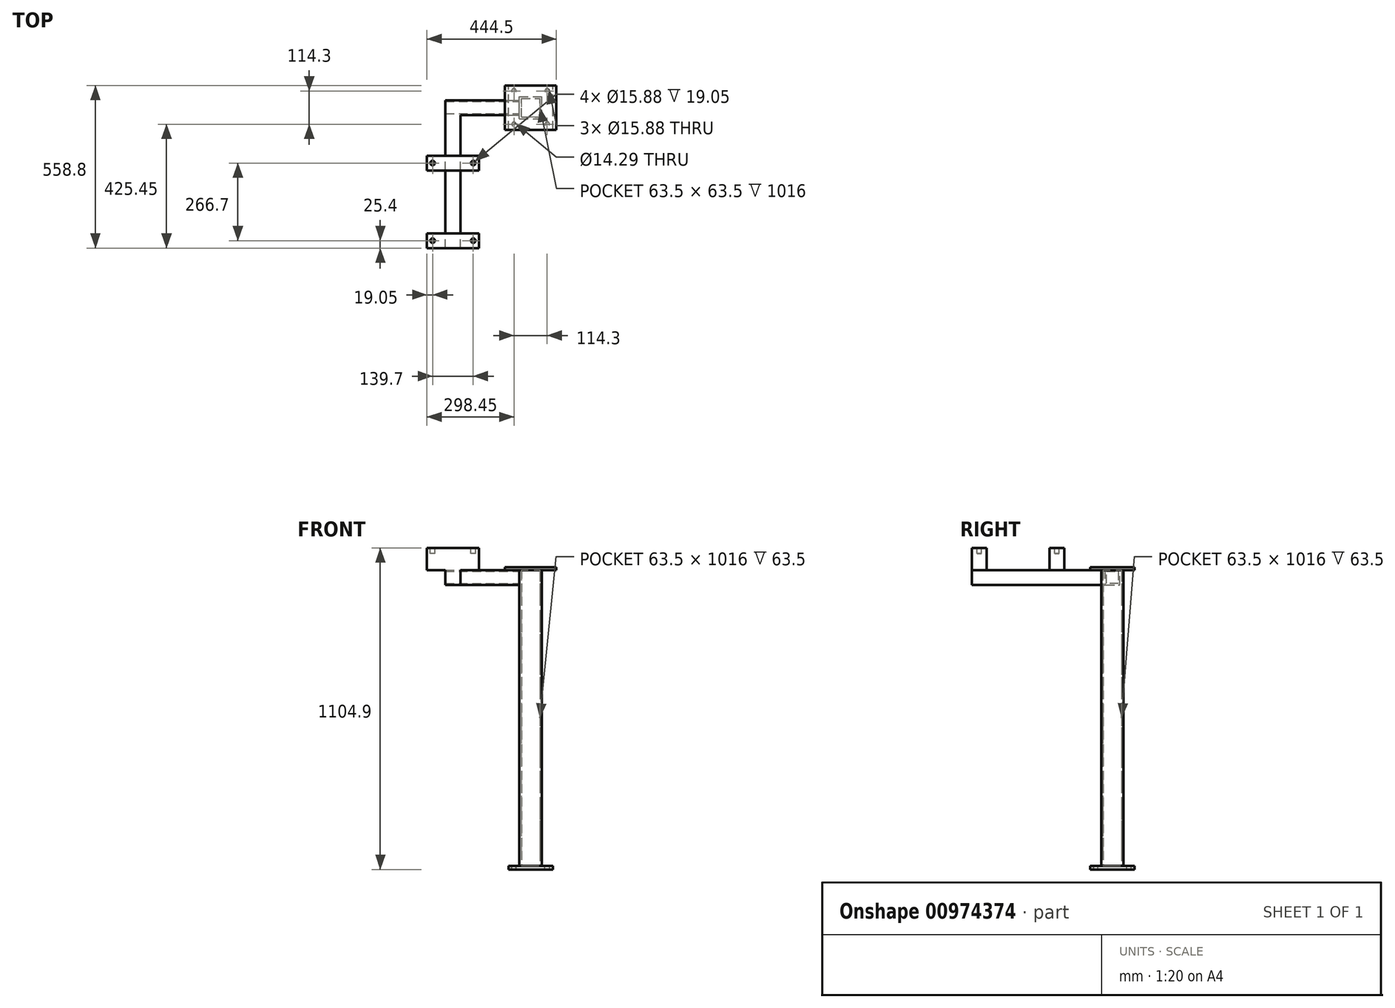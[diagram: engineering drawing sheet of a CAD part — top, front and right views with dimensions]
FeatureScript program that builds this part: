
annotation { "Feature Type Name" : "Feature", "Feature Type Description" : "" }
export const myFeature = defineFeature(function(context is Context, id is Id, definition is map)
    precondition{}
    {
        {
            var Q0;
            Q0=qCreatedBy(makeId("Top.planeOp"),FACE);
            var sketch = newSketch(context, id + "F0", { "sketchPlane" : qUnion([Q0])});
            skLineSegment(sketch, "E0.bottom", {"start": v(0, 0) * mm, "end": v(152.4, 0) * mm});
            skLineSegment(sketch, "E0.top", {"start": v(0, 152.4) * mm, "end": v(152.4, 152.4) * mm});
            skLineSegment(sketch, "E0.left", {"start": v(0, 0) * mm, "end": v(0, 152.4) * mm});
            skLineSegment(sketch, "E0.right", {"start": v(152.4, 0) * mm, "end": v(152.4, 152.4) * mm});
            skSolve(sketch);
        }
        {
            var Q0;
            Q0 = qSketchRegion(id + "F0", true);
            extrude(context, id + "F1", {"entities" : qUnion([Q0]), "depth" : 12.7 * mm, "offsetDistance" : 25.4 * mm});
        }
        {
            var Q0;
            Q0=makeQuery(id+"F1.opExtrude","CAP_FACE",FACE,{"disambiguationData":[OSD([sQuery(id+"F0.wireOp",EDGE,"E0.bottom"),sQuery(id+"F0.wireOp",EDGE,"E0.top"),sQuery(id+"F0.wireOp",EDGE,"E0.left"),sQuery(id+"F0.wireOp",EDGE,"E0.right")])],"isStart":false});
            var sketch = newSketch(context, id + "F2", { "sketchPlane" : qUnion([Q0])});
            skLineSegment(sketch, "E1.bottom", {"start": v(38.1, 38.1) * mm, "end": v(114.3, 38.1) * mm});
            skLineSegment(sketch, "E1.top", {"start": v(38.1, 114.3) * mm, "end": v(114.3, 114.3) * mm});
            skLineSegment(sketch, "E1.left", {"start": v(38.1, 38.1) * mm, "end": v(38.1, 114.3) * mm});
            skLineSegment(sketch, "E1.right", {"start": v(114.3, 38.1) * mm, "end": v(114.3, 114.3) * mm});
            skLineSegment(sketch, "E2.bottom", {"start": v(44.45, 44.45) * mm, "end": v(107.95, 44.45) * mm});
            skLineSegment(sketch, "E2.top", {"start": v(44.45, 107.95) * mm, "end": v(107.95, 107.95) * mm});
            skLineSegment(sketch, "E2.left", {"start": v(44.45, 44.45) * mm, "end": v(44.45, 107.95) * mm});
            skLineSegment(sketch, "E2.right", {"start": v(107.95, 44.45) * mm, "end": v(107.95, 107.95) * mm});
            skSolve(sketch);
        }
        {
            var Q0;
            Q0 = qSketchRegion(id + "F2", true);
            extrude(context, id + "F3", {"entities" : qUnion([Q0]), "operationType" : NewBodyOperationType.ADD, "depth" : 1016 * mm, "offsetDistance" : 25.4 * mm});
        }
        {
            var Q0;
            Q0=makeQuery(id+"F3.opExtrude","SWEPT_FACE",FACE,{"disambiguationData":[OSD([sQuery(id+"F2.wireOp",EDGE,"E1.left")])]});
            var sketch = newSketch(context, id + "F4", { "sketchPlane" : qUnion([Q0])});
            skLineSegment(sketch, "E3", {"start": v(-114.3, 1028.7) * mm, "end": v(-101.6, 1028.7) * mm});
            skLineSegment(sketch, "E4", {"start": v(-101.6, 1028.7) * mm, "end": v(0, 1028.7) * mm});
            skLineSegment(sketch, "E5", {"start": v(-101.6, 1028.7) * mm, "end": v(-50.8, 1028.7) * mm});
            skLineSegment(sketch, "E6", {"start": v(-50.8, 1028.7) * mm, "end": v(-50.8, 977.9) * mm});
            skLineSegment(sketch, "E7", {"start": v(-50.8, 977.9) * mm, "end": v(-101.6, 977.9) * mm});
            skLineSegment(sketch, "E8", {"start": v(-101.6, 977.9) * mm, "end": v(-101.6, 1028.7) * mm});
            skLineSegment(sketch, "E9", {"start": v(-101.6, 1028.7) * mm, "end": v(-101.6, 1023.94) * mm});
            skLineSegment(sketch, "E10", {"start": v(-101.6, 1023.94) * mm, "end": v(-96.84, 1023.94) * mm});
            skLineSegment(sketch, "E11", {"start": v(-96.84, 1023.94) * mm, "end": v(-96.84, 982.66) * mm});
            skLineSegment(sketch, "E12", {"start": v(-96.84, 982.66) * mm, "end": v(-55.56, 982.66) * mm});
            skLineSegment(sketch, "E13", {"start": v(-55.56, 982.66) * mm, "end": v(-55.56, 1023.94) * mm});
            skLineSegment(sketch, "E14", {"start": v(-55.56, 1023.94) * mm, "end": v(-96.84, 1023.94) * mm});
            skSolve(sketch);
        }
        {
            var Q0;
            Q0 = qSketchRegion(id + "F4", true);
            extrude(context, id + "F5", {"entities" : qUnion([Q0]), "operationType" : NewBodyOperationType.ADD, "depth" : 254 * mm, "offsetDistance" : 25.4 * mm});
        }
        {
            var Q0;
            Q0=makeQuery(id+"F5.opExtrude","SWEPT_FACE",FACE,{"disambiguationData":[OSD([sQuery(id+"F4.wireOp",EDGE,"E6")])]});
            var sketch = newSketch(context, id + "F6", { "sketchPlane" : qUnion([Q0])});
            skLineSegment(sketch, "E15", {"start": v(-215.9, 1028.7) * mm, "end": v(-165.1, 1028.7) * mm});
            skLineSegment(sketch, "E16", {"start": v(-165.1, 1028.7) * mm, "end": v(-165.1, 977.9) * mm});
            skLineSegment(sketch, "E17", {"start": v(-165.1, 977.9) * mm, "end": v(-215.9, 977.9) * mm});
            skLineSegment(sketch, "E18", {"start": v(-215.9, 977.9) * mm, "end": v(-215.9, 1028.7) * mm});
            skSolve(sketch);
        }
        {
            var Q0;
            Q0 = qSketchRegion(id + "F6", true);
            extrude(context, id + "F7", {"entities" : qUnion([Q0]), "operationType" : NewBodyOperationType.ADD, "depth" : 457.2 * mm, "offsetDistance" : 25.4 * mm});
        }
        {
            var Q0;
            Q0=makeQuery(id+"F7.boolean.opBoolean","MERGE",FACE,{"derivedFrom":[makeQuery(id+"F5.boolean.opBoolean","MERGE",FACE,{"derivedFrom":[makeQuery(id+"F3.opExtrude","CAP_FACE",FACE,{"disambiguationData":[OSD([sQuery(id+"F2.wireOp",EDGE,"E1.bottom"),sQuery(id+"F2.wireOp",EDGE,"E1.top"),sQuery(id+"F2.wireOp",EDGE,"E1.left"),sQuery(id+"F2.wireOp",EDGE,"E1.right"),sQuery(id+"F2.wireOp",EDGE,"E2.bottom"),sQuery(id+"F2.wireOp",EDGE,"E2.top"),sQuery(id+"F2.wireOp",EDGE,"E2.left"),sQuery(id+"F2.wireOp",EDGE,"E2.right")])],"isStart":false}),makeQuery(id+"F5.opExtrude","SWEPT_FACE",FACE,{"disambiguationData":[OSD([sQuery(id+"F4.wireOp",EDGE,"E5")])]})]}),makeQuery(id+"F7.opExtrude","SWEPT_FACE",FACE,{"disambiguationData":[OSD([sQuery(id+"F6.wireOp",EDGE,"E15")])]})]});
            var sketch = newSketch(context, id + "F8", { "sketchPlane" : qUnion([Q0])});
            skLineSegment(sketch, "E19", {"start": v(-165.1, 50.8) * mm, "end": v(-165.1, -88.9) * mm});
            skLineSegment(sketch, "E20", {"start": v(-165.1, -88.9) * mm, "end": v(-101.6, -88.9) * mm});
            skLineSegment(sketch, "E21", {"start": v(-101.6, -88.9) * mm, "end": v(-101.6, -139.7) * mm});
            skLineSegment(sketch, "E22", {"start": v(-101.6, -139.7) * mm, "end": v(-279.4, -139.7) * mm});
            skLineSegment(sketch, "E23", {"start": v(-279.4, -139.7) * mm, "end": v(-279.4, -88.9) * mm});
            skLineSegment(sketch, "E24", {"start": v(-279.4, -88.9) * mm, "end": v(-165.1, -88.9) * mm});
            skLineSegment(sketch, "E25", {"start": v(-101.6, -139.7) * mm, "end": v(-101.6, -355.6) * mm});
            skLineSegment(sketch, "E26", {"start": v(-101.6, -355.6) * mm, "end": v(-279.4, -355.6) * mm});
            skLineSegment(sketch, "E27", {"start": v(-279.4, -355.6) * mm, "end": v(-279.4, -406.4) * mm});
            skLineSegment(sketch, "E28", {"start": v(-279.4, -406.4) * mm, "end": v(-101.6, -406.4) * mm});
            skLineSegment(sketch, "E29", {"start": v(-101.6, -406.4) * mm, "end": v(-101.6, -355.6) * mm});
            skSolve(sketch);
        }
        {
            var Q0;
            Q0 = qSketchRegion(id + "F8", true);
            extrude(context, id + "F9", {"entities" : qUnion([Q0]), "operationType" : NewBodyOperationType.ADD, "depth" : 76.2 * mm, "offsetDistance" : 25.4 * mm});
        }
        {
            var Q0;
            {var subQ0=sQuery(id+"F2.wireOp",EDGE,"E2.right");var subQ4=sQuery(id+"F2.wireOp",EDGE,"E2.left");var subQ7=sQuery(id+"F4.wireOp",EDGE,"E5");var subQ8=sQuery(id+"F2.wireOp",EDGE,"E2.top");var subQ9=sQuery(id+"F2.wireOp",EDGE,"E2.bottom");var subQ10=sQuery(id+"F2.wireOp",EDGE,"E1.bottom");var subQ11=sQuery(id+"F2.wireOp",EDGE,"E1.right");var subQ12=sQuery(id+"F2.wireOp",EDGE,"E1.top");var subQ13=sQuery(id+"F2.wireOp",EDGE,"E1.left");Q0=makeQuery(id+"F9.boolean.opBoolean","SPLIT",FACE,{"disambiguationData":[TD([makeQuery(id+"F3.opExtrude","SWEPT_FACE",FACE,{"disambiguationData":[OSD([subQ10])]})])],"derivedFrom":makeQuery(id+"F7.boolean.opBoolean","MERGE",FACE,{"derivedFrom":[makeQuery(id+"F5.boolean.opBoolean","MERGE",FACE,{"derivedFrom":[makeQuery(id+"F3.opExtrude","CAP_FACE",FACE,{"disambiguationData":[OSD([subQ10,subQ12,subQ13,subQ11,subQ9,subQ8,subQ4,subQ0])],"isStart":false}),makeQuery(id+"F5.opExtrude","SWEPT_FACE",FACE,{"disambiguationData":[OSD([subQ7])]})]}),makeQuery(id+"F7.opExtrude","SWEPT_FACE",FACE,{"disambiguationData":[OSD([sQuery(id+"F6.wireOp",EDGE,"E15")])]})]})});}
            var sketch = newSketch(context, id + "F10", { "sketchPlane" : qUnion([Q0])});
            skLineSegment(sketch, "E30", {"start": v(114.3, 114.3) * mm, "end": v(114.3, 152.4) * mm});
            skLineSegment(sketch, "E31", {"start": v(114.3, 152.4) * mm, "end": v(165.1, 152.4) * mm});
            skLineSegment(sketch, "E32", {"start": v(165.1, 152.4) * mm, "end": v(165.1, 0) * mm});
            skLineSegment(sketch, "E33", {"start": v(165.1, 0) * mm, "end": v(-12.7, 0) * mm});
            skLineSegment(sketch, "E34", {"start": v(-12.7, 0) * mm, "end": v(-12.7, 152.4) * mm});
            skLineSegment(sketch, "E35", {"start": v(-12.7, 152.4) * mm, "end": v(165.1, 152.4) * mm});
            skSolve(sketch);
        }
        {
            var Q0;
            Q0 = qSketchRegion(id + "F10", true);
            extrude(context, id + "F11", {"entities" : qUnion([Q0]), "operationType" : NewBodyOperationType.ADD, "depth" : 9.52 * mm, "offsetDistance" : 25.4 * mm});
        }
        {
            var Q0;
            Q0=makeQuery(id+"F9.opExtrude","CAP_FACE",FACE,{"disambiguationData":[OSD([sQuery(id+"F8.wireOp",EDGE,"E20"),sQuery(id+"F8.wireOp",EDGE,"E21"),sQuery(id+"F8.wireOp",EDGE,"E22"),sQuery(id+"F8.wireOp",EDGE,"E23"),sQuery(id+"F8.wireOp",EDGE,"E24")])],"isStart":false});
            var sketch = newSketch(context, id + "F12", { "sketchPlane" : qUnion([Q0])});
            skLineSegment(sketch, "E36", {"start": v(-279.4, -114.3) * mm, "end": v(-101.6, -114.3) * mm});
            skLineSegment(sketch, "E37", {"start": v(-101.6, -114.3) * mm, "end": v(-120.65, -114.3) * mm});
            skLineSegment(sketch, "E38", {"start": v(-279.4, -114.3) * mm, "end": v(-260.35, -114.3) * mm});
            skCircle(sketch, "E39", {"center": v(-260.35, -114.3) * mm, "radius": 7.94 * mm});
            skCircle(sketch, "E40", {"center": v(-120.65, -114.3) * mm, "radius": 7.94 * mm});
            skSolve(sketch);
        }
        {
            var Q0;
            Q0 = qSketchRegion(id + "F12", true);
            extrude(context, id + "F13", {"entities" : qUnion([Q0]), "operationType" : NewBodyOperationType.REMOVE, "oppositeDirection" : true, "depth" : 19.05 * mm, "offsetDistance" : 25.4 * mm});
        }
        {
            var Q0;
            Q0=makeQuery(id+"F9.opExtrude","CAP_FACE",FACE,{"disambiguationData":[OSD([sQuery(id+"F8.wireOp",EDGE,"E26"),sQuery(id+"F8.wireOp",EDGE,"E27"),sQuery(id+"F8.wireOp",EDGE,"E28"),sQuery(id+"F8.wireOp",EDGE,"E29")])],"isStart":false});
            var sketch = newSketch(context, id + "F14", { "sketchPlane" : qUnion([Q0])});
            skLineSegment(sketch, "E41", {"start": v(-279.4, -381) * mm, "end": v(-101.6, -381) * mm});
            skLineSegment(sketch, "E42", {"start": v(-279.4, -381) * mm, "end": v(-260.35, -381) * mm});
            skLineSegment(sketch, "E43", {"start": v(-101.6, -381) * mm, "end": v(-120.65, -381) * mm});
            skCircle(sketch, "E44", {"center": v(-260.35, -381) * mm, "radius": 7.94 * mm});
            skCircle(sketch, "E45", {"center": v(-120.65, -381) * mm, "radius": 7.94 * mm});
            skSolve(sketch);
        }
        {
            var Q0;
            Q0 = qSketchRegion(id + "F14", true);
            extrude(context, id + "F15", {"entities" : qUnion([Q0]), "operationType" : NewBodyOperationType.REMOVE, "oppositeDirection" : true, "depth" : 19.05 * mm, "offsetDistance" : 25.4 * mm});
        }
        {
            var Q0;
            {var subQ0=sQuery(id+"F0.wireOp",EDGE,"E0.left");var subQ1=sQuery(id+"F0.wireOp",EDGE,"E0.top");var subQ2=sQuery(id+"F0.wireOp",EDGE,"E0.right");var subQ3=sQuery(id+"F0.wireOp",EDGE,"E0.bottom");Q0=makeQuery(id+"F3.boolean.opBoolean","SPLIT",FACE,{"disambiguationData":[TD([makeQuery(id+"F1.opExtrude","SWEPT_FACE",FACE,{"disambiguationData":[OSD([subQ3])]})])],"derivedFrom":makeQuery(id+"F1.opExtrude","CAP_FACE",FACE,{"disambiguationData":[OSD([subQ3,subQ1,subQ0,subQ2])],"isStart":false})});}
            var sketch = newSketch(context, id + "F16", { "sketchPlane" : qUnion([Q0])});
            skLineSegment(sketch, "E46", {"start": v(0, 0) * mm, "end": v(19.05, 0) * mm});
            skLineSegment(sketch, "E47", {"start": v(19.05, 0) * mm, "end": v(19.05, 19.05) * mm});
            skCircle(sketch, "E48", {"center": v(19.05, 19.05) * mm, "radius": 7.14 * mm});
            skLineSegment(sketch, "E49", {"start": v(0, 152.4) * mm, "end": v(19.05, 152.4) * mm});
            skLineSegment(sketch, "E50", {"start": v(19.05, 152.4) * mm, "end": v(19.05, 133.35) * mm});
            skLineSegment(sketch, "E51", {"start": v(152.4, 0) * mm, "end": v(152.4, 19.05) * mm});
            skLineSegment(sketch, "E52", {"start": v(152.4, 19.05) * mm, "end": v(133.35, 19.05) * mm});
            skLineSegment(sketch, "E53", {"start": v(152.4, 152.4) * mm, "end": v(133.35, 152.4) * mm});
            skLineSegment(sketch, "E54", {"start": v(133.35, 152.4) * mm, "end": v(133.35, 133.35) * mm});
            skCircle(sketch, "E55", {"center": v(133.35, 133.35) * mm, "radius": 7.94 * mm});
            skCircle(sketch, "E56", {"center": v(133.35, 19.05) * mm, "radius": 7.94 * mm});
            skCircle(sketch, "E57", {"center": v(19.05, 133.35) * mm, "radius": 7.94 * mm});
            skSolve(sketch);
        }
        {
            var Q0;
            Q0 = qSketchRegion(id + "F16", true);
            extrude(context, id + "F17", {"entities" : qUnion([Q0]), "operationType" : NewBodyOperationType.REMOVE, "oppositeDirection" : true, "depth" : 25.4 * mm, "offsetDistance" : 25.4 * mm});
        }
    });
